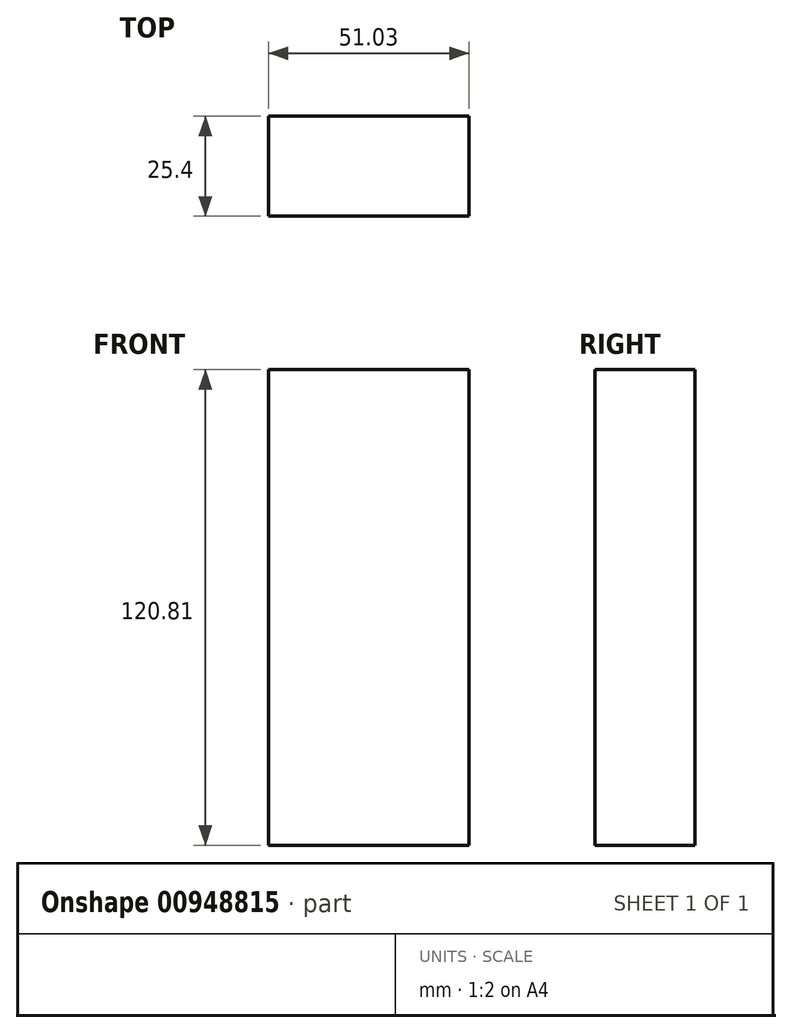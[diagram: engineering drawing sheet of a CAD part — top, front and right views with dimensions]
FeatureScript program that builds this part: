
annotation { "Feature Type Name" : "Feature", "Feature Type Description" : "" }
export const myFeature = defineFeature(function(context is Context, id is Id, definition is map)
    precondition{}
    {
        {
            var Q0;
            Q0=qCreatedBy(makeId("Front.planeOp"),FACE);
            var sketch = newSketch(context, id + "F0", { "sketchPlane" : qUnion([Q0])});
            skLineSegment(sketch, "E0", {"start": v(-52.83, -64.96) * mm, "end": v(-58.9, 38.54) * mm});
            skLineSegment(sketch, "E1.bottom", {"start": v(0, 46.9) * mm, "end": v(51.03, 46.9) * mm});
            skLineSegment(sketch, "E1.top", {"start": v(0, -73.9) * mm, "end": v(51.03, -73.9) * mm});
            skLineSegment(sketch, "E1.left", {"start": v(0, 46.9) * mm, "end": v(0, -73.9) * mm});
            skLineSegment(sketch, "E1.right", {"start": v(51.03, 46.9) * mm, "end": v(51.03, -73.9) * mm});
            skSolve(sketch);
        }
        {
            var Q0;
            Q0=makeQuery(id+"F0.imprint","IMPRINT",FACE,{"disambiguationData":[TD([[makeQuery(id+"F0.imprint","IMPRINT",EDGE,{"derivedFrom":sQuery(id+"F0.wireOp",EDGE,"E1.bottom")}),-1.0]])]});
            extrude(context, id + "F1", {"entities" : qUnion([Q0]), "depth" : 25.4 * mm, "offsetDistance" : 25.4 * mm});
        }
    });
